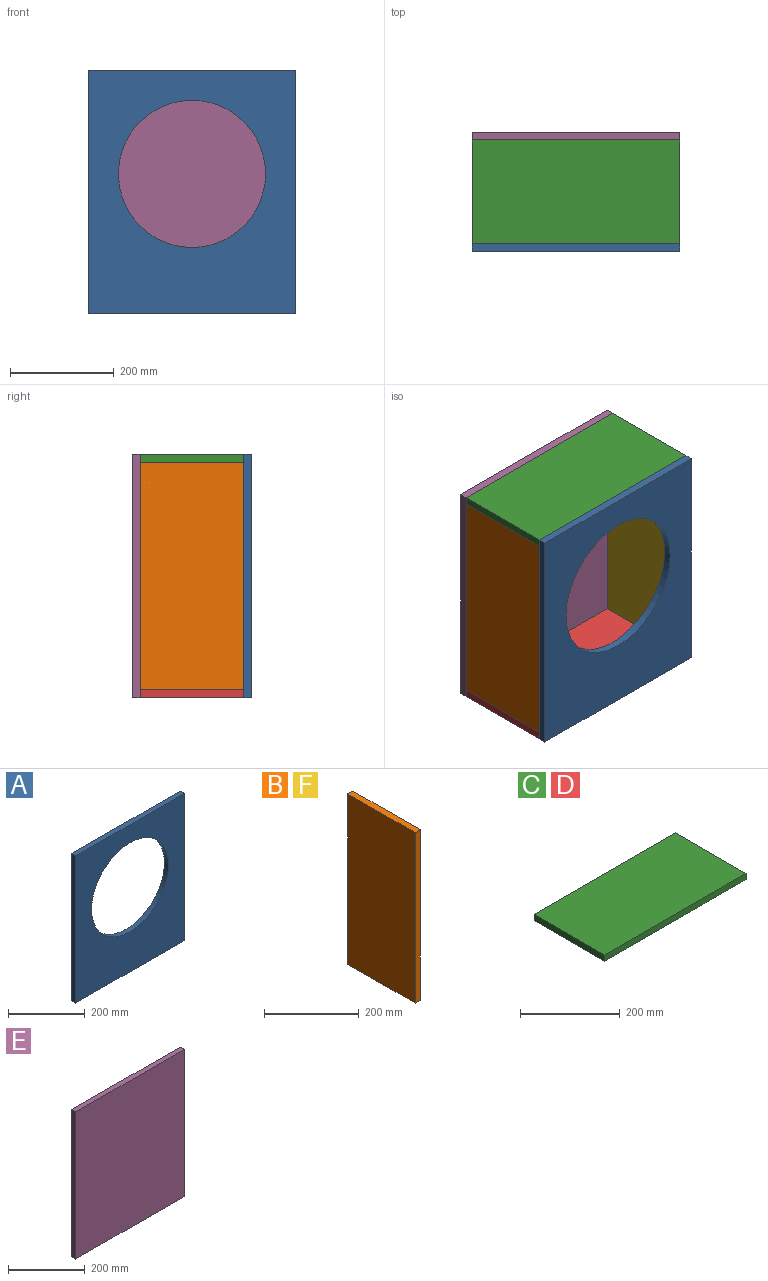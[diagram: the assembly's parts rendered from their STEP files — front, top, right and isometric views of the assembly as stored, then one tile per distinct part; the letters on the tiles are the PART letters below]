
ASSEMBLY  parts=6 mates=6
PART A: 7 faces, bbox 400x15x470 mm
  f0: plane 400x15mm, normal (0,0,1), area 6000mm2, adj f1,f4,f5,f6
  f1: plane 470x15mm, normal (-1,0,0), area 7050mm2, adj f0,f2,f5,f6
  f2: plane 400x15mm, normal (0,0,-1), area 6000mm2, adj f1,f4,f5,f6
  f3: cylinder r=142mm len=284mm, axis (0,1,0), area 13383.2mm2, adj f5,f6
  f4: plane 470x15mm, normal (1,0,0), area 7050mm2, adj f0,f2,f5,f6
  f5: plane 470x400mm, normal (0,-1,0), area 124652.9mm2, adj f0,f1,f2,f3,f4
  f6: plane 470x400mm, normal (0,1,0), area 124652.9mm2, adj f0,f1,f2,f3,f4
PART B: 6 faces, bbox 15x200x440 mm
  f0: plane 200x15mm, normal (0,0,1), area 3000mm2, adj f1,f3,f4,f5
  f1: plane 440x15mm, normal (0,-1,0), area 6600mm2, adj f0,f2,f4,f5
  f2: plane 200x15mm, normal (0,0,-1), area 3000mm2, adj f1,f3,f4,f5
  f3: plane 440x15mm, normal (0,1,0), area 6600mm2, adj f0,f2,f4,f5
  f4: plane 440x200mm, normal (1,0,0), area 88000mm2, adj f0,f1,f2,f3
  f5: plane 440x200mm, normal (-1,0,0), area 88000mm2, adj f0,f1,f2,f3
PART C: 6 faces, bbox 400x200x15 mm
  f0: plane 400x15mm, normal (0,1,0), area 6000mm2, adj f1,f3,f4,f5
  f1: plane 200x15mm, normal (-1,0,0), area 3000mm2, adj f0,f2,f4,f5
  f2: plane 400x15mm, normal (0,-1,0), area 6000mm2, adj f1,f3,f4,f5
  f3: plane 200x15mm, normal (1,0,0), area 3000mm2, adj f0,f2,f4,f5
  f4: plane 400x200mm, normal (0,0,1), area 80000mm2, adj f0,f1,f2,f3
  f5: plane 400x200mm, normal (0,0,-1), area 80000mm2, adj f0,f1,f2,f3
PART D: same geometry as C
PART E: 6 faces, bbox 400x15x470 mm
  f0: plane 400x15mm, normal (0,0,1), area 6000mm2, adj f1,f3,f4,f5
  f1: plane 470x15mm, normal (-1,0,0), area 7050mm2, adj f0,f2,f4,f5
  f2: plane 400x15mm, normal (0,0,-1), area 6000mm2, adj f1,f3,f4,f5
  f3: plane 470x15mm, normal (1,0,0), area 7050mm2, adj f0,f2,f4,f5
  f4: plane 470x400mm, normal (0,-1,0), area 188000mm2, adj f0,f1,f2,f3
  f5: plane 470x400mm, normal (0,1,0), area 188000mm2, adj f0,f1,f2,f3
PART F: same geometry as B
PLACE A t=(-209.11,23.01,-203.85)mm
PLACE B t=(-209.11,23.01,-188.85)mm
PLACE C t=(-209.11,23.01,251.15)mm
PLACE D t=(-209.11,23.01,-203.85)mm
PLACE E t=(-209.11,238.01,-203.85)mm
PLACE F t=(175.89,23.01,-188.85)mm
MATE parallel F.f1 <-> A.f6  axis (0,-1,0) through (190.89,23.01,31.15)mm
MATE parallel E.f4 <-> F.f3  axis (0,-1,0) through (190.89,223.01,31.15)mm
MATE parallel F.f1 <-> A.f6  axis (0,-1,0) through (190.89,23.01,31.15)mm
MATE parallel C.f2 <-> A.f6  axis (0,-1,0) through (-9.11,23.01,266.15)mm
MATE parallel B.f1 <-> A.f6  axis (0,-1,0) through (-209.11,23.01,31.15)mm
MATE parallel D.f2 <-> A.f6  axis (0,-1,0) through (-9.11,23.01,-203.85)mm
